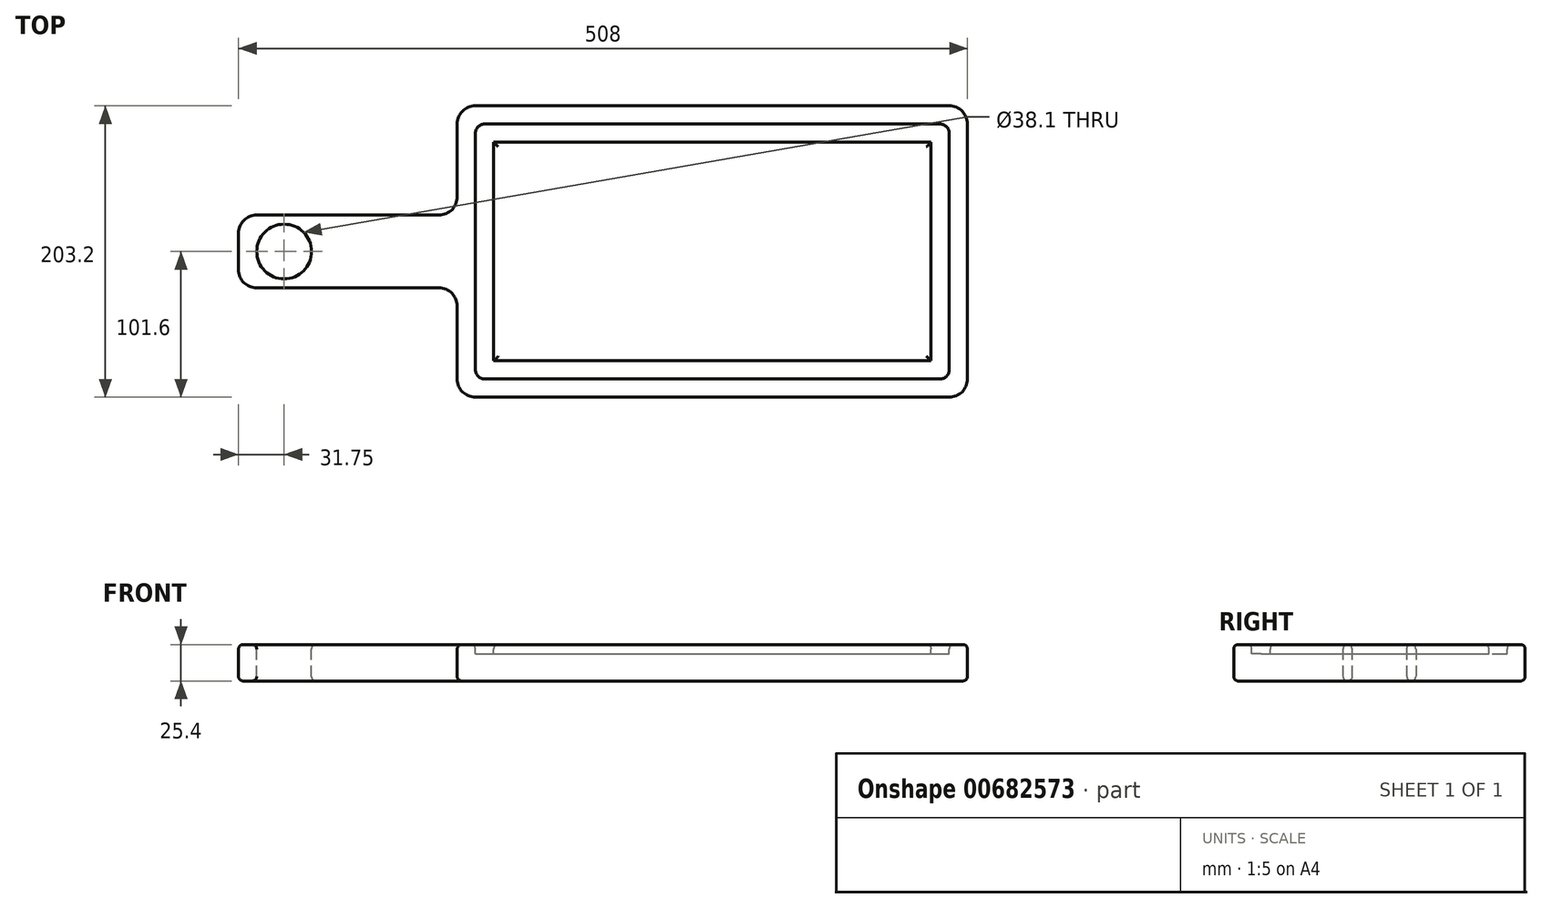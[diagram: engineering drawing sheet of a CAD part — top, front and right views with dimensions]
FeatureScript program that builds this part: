
annotation { "Feature Type Name" : "Feature", "Feature Type Description" : "" }
export const myFeature = defineFeature(function(context is Context, id is Id, definition is map)
    precondition{}
    {
        {
            var Q0;
            Q0=qCreatedBy(makeId("Top.planeOp"),FACE);
            var sketch = newSketch(context, id + "F0", { "sketchPlane" : qUnion([Q0])});
            skLineSegment(sketch, "E0.bottom", {"start": v(0, 0) * mm, "end": v(355.6, 0) * mm});
            skLineSegment(sketch, "E0.top", {"start": v(0, 203.2) * mm, "end": v(355.6, 203.2) * mm});
            skLineSegment(sketch, "E0.left", {"start": v(0, 0) * mm, "end": v(0, 203.2) * mm});
            skLineSegment(sketch, "E0.right", {"start": v(355.6, 0) * mm, "end": v(355.6, 203.2) * mm});
            skLineSegment(sketch, "E1.bottom", {"start": v(0, 127) * mm, "end": v(-152.4, 127) * mm});
            skLineSegment(sketch, "E1.top", {"start": v(0, 76.2) * mm, "end": v(-152.4, 76.2) * mm});
            skLineSegment(sketch, "E1.left", {"start": v(0, 127) * mm, "end": v(0, 76.2) * mm});
            skLineSegment(sketch, "E1.right", {"start": v(-152.4, 127) * mm, "end": v(-152.4, 76.2) * mm});
            skSolve(sketch);
        }
        {
            var Q0;
            {var subQ3=sQuery(id+"F0.wireOp",EDGE,"E0.bottom");Q0=makeQuery(id+"F0.imprint","IMPRINT",FACE,{"disambiguationData":[TD([[makeQuery(id+"F0.imprint","IMPRINT",EDGE,{"derivedFrom":subQ3}),1.0]])]});}
            var Q1;
            Q1=makeQuery(id+"F0.imprint","IMPRINT",FACE,{"disambiguationData":[TD([[makeQuery(id+"F0.imprint","IMPRINT",EDGE,{"derivedFrom":sQuery(id+"F0.wireOp",EDGE,"E1.bottom")}),1.0]])]});
            extrude(context, id + "F1", {"entities" : qUnion([Q0, Q1]), "depth" : 25.4 * mm, "offsetDistance" : 25.4 * mm});
        }
        {
            var Q0;
            Q0=makeQuery(id+"F1.opExtrude","CAP_FACE",FACE,{"disambiguationData":[OSD([sQuery(id+"F0.wireOp",EDGE,"E0.bottom"),sQuery(id+"F0.wireOp",EDGE,"E0.top"),sQuery(id+"F0.wireOp",EDGE,"E0.left"),sQuery(id+"F0.wireOp",EDGE,"E0.right"),sQuery(id+"F0.wireOp",EDGE,"E1.bottom"),sQuery(id+"F0.wireOp",EDGE,"E1.top"),sQuery(id+"F0.wireOp",EDGE,"E1.right")])],"isStart":false});
            var sketch = newSketch(context, id + "F2", { "sketchPlane" : qUnion([Q0])});
            skCircle(sketch, "E2", {"center": v(-120.65, 101.6) * mm, "radius": 19.05 * mm});
            skSolve(sketch);
        }
        {
            var Q0;
            Q0 = qSketchRegion(id + "F2", true);
            extrude(context, id + "F3", {"entities" : qUnion([Q0]), "operationType" : NewBodyOperationType.REMOVE, "oppositeDirection" : true, "depth" : 25.4 * mm, "offsetDistance" : 25.4 * mm});
        }
        {
            var Q0;
            Q0=makeQuery(id+"F1.opExtrude","CAP_FACE",FACE,{"disambiguationData":[OSD([sQuery(id+"F0.wireOp",EDGE,"E0.bottom"),sQuery(id+"F0.wireOp",EDGE,"E0.top"),sQuery(id+"F0.wireOp",EDGE,"E0.left"),sQuery(id+"F0.wireOp",EDGE,"E0.right"),sQuery(id+"F0.wireOp",EDGE,"E1.bottom"),sQuery(id+"F0.wireOp",EDGE,"E1.top"),sQuery(id+"F0.wireOp",EDGE,"E1.right")])],"isStart":false});
            var sketch = newSketch(context, id + "F4", { "sketchPlane" : qUnion([Q0])});
            skLineSegment(sketch, "E3.0", {"start": v(12.7, 12.7) * mm, "end": v(12.7, 76.2) * mm});
            skLineSegment(sketch, "E3.1", {"start": v(12.7, 127) * mm, "end": v(12.7, 190.5) * mm});
            skLineSegment(sketch, "E3.2", {"start": v(12.7, 190.5) * mm, "end": v(342.9, 190.5) * mm});
            skLineSegment(sketch, "E3.3", {"start": v(342.9, 12.7) * mm, "end": v(342.9, 190.5) * mm});
            skLineSegment(sketch, "E3.4", {"start": v(12.7, 12.7) * mm, "end": v(342.9, 12.7) * mm});
            skLineSegment(sketch, "E4", {"start": v(12.7, 127) * mm, "end": v(12.7, 76.2) * mm});
            skLineSegment(sketch, "E5.0", {"start": v(25.4, 127) * mm, "end": v(25.4, 177.8) * mm});
            skLineSegment(sketch, "E5.1", {"start": v(330.2, 25.4) * mm, "end": v(330.2, 177.8) * mm});
            skLineSegment(sketch, "E5.2", {"start": v(25.4, 25.4) * mm, "end": v(330.2, 25.4) * mm});
            skLineSegment(sketch, "E5.3", {"start": v(25.4, 177.8) * mm, "end": v(330.2, 177.8) * mm});
            skLineSegment(sketch, "E5.4", {"start": v(25.4, 25.4) * mm, "end": v(25.4, 76.2) * mm});
            skLineSegment(sketch, "E5.5", {"start": v(25.4, 127) * mm, "end": v(25.4, 76.2) * mm});
            skSolve(sketch);
        }
        {
            var Q0;
            Q0=makeQuery(id+"F4.imprint","IMPRINT",FACE,{"disambiguationData":[TD([[makeQuery(id+"F4.imprint","IMPRINT",EDGE,{"derivedFrom":sQuery(id+"F4.wireOp",EDGE,"E3.0")}),-1.0]])]});
            extrude(context, id + "F5", {"entities" : qUnion([Q0]), "operationType" : NewBodyOperationType.REMOVE, "oppositeDirection" : true, "depth" : 6.35 * mm, "offsetDistance" : 25.4 * mm});
        }
        {
            var Q0;
            Q0=makeQuery(id+"F5.boolean.opBoolean","COPY",EDGE,{"derivedFrom":makeQuery(id+"F5.opExtrude","SWEPT_EDGE",EDGE,{"disambiguationData":[OSD([sQuery(id+"F4.wireOp",EDGE,"E3.1"),sQuery(id+"F4.wireOp",EDGE,"E3.2")])]})});
            var Q1;
            Q1=makeQuery(id+"F5.boolean.opBoolean","COPY",EDGE,{"derivedFrom":makeQuery(id+"F5.opExtrude","SWEPT_EDGE",EDGE,{"disambiguationData":[OSD([sQuery(id+"F4.wireOp",EDGE,"E3.2"),sQuery(id+"F4.wireOp",EDGE,"E3.3")])]})});
            var Q2;
            Q2=makeQuery(id+"F5.boolean.opBoolean","COPY",EDGE,{"derivedFrom":makeQuery(id+"F5.opExtrude","SWEPT_EDGE",EDGE,{"disambiguationData":[OSD([sQuery(id+"F4.wireOp",EDGE,"E3.3"),sQuery(id+"F4.wireOp",EDGE,"E3.4")])]})});
            var Q3;
            Q3=makeQuery(id+"F5.boolean.opBoolean","COPY",EDGE,{"derivedFrom":makeQuery(id+"F5.opExtrude","SWEPT_EDGE",EDGE,{"disambiguationData":[OSD([sQuery(id+"F4.wireOp",EDGE,"E3.0"),sQuery(id+"F4.wireOp",EDGE,"E3.4")])]})});
            fillet(context, id + "F6", {"entities" : qUnion([Q0, Q1, Q2, Q3]), "radius" : 6.35 * mm, "tangentPropagation" : true, "allowEdgeOverflow" : false});
        }
        {
            var Q0;
            Q0=makeQuery(id+"F1.opExtrude","SWEPT_EDGE",EDGE,{"disambiguationData":[OSD([sQuery(id+"F0.wireOp",EDGE,"E0.bottom"),sQuery(id+"F0.wireOp",EDGE,"E0.left")])]});
            var Q1;
            Q1=makeQuery(id+"F1.opExtrude","SWEPT_EDGE",EDGE,{"disambiguationData":[OSD([sQuery(id+"F0.wireOp",EDGE,"E1.top"),sQuery(id+"F0.wireOp",EDGE,"E1.right")])]});
            var Q2;
            Q2=makeQuery(id+"F1.opExtrude","SWEPT_EDGE",EDGE,{"disambiguationData":[OSD([sQuery(id+"F0.wireOp",EDGE,"E1.bottom"),sQuery(id+"F0.wireOp",EDGE,"E1.right")])]});
            var Q3;
            Q3=makeQuery(id+"F1.opExtrude","SWEPT_EDGE",EDGE,{"disambiguationData":[OSD([sQuery(id+"F0.wireOp",EDGE,"E0.top"),sQuery(id+"F0.wireOp",EDGE,"E0.left")])]});
            var Q4;
            Q4=makeQuery(id+"F1.opExtrude","SWEPT_EDGE",EDGE,{"disambiguationData":[OSD([sQuery(id+"F0.wireOp",EDGE,"E0.top"),sQuery(id+"F0.wireOp",EDGE,"E0.right")])]});
            var Q5;
            Q5=makeQuery(id+"F1.opExtrude","SWEPT_EDGE",EDGE,{"disambiguationData":[OSD([sQuery(id+"F0.wireOp",EDGE,"E0.bottom"),sQuery(id+"F0.wireOp",EDGE,"E0.right")])]});
            fillet(context, id + "F7", {"entities" : qUnion([Q0, Q1, Q2, Q3, Q4, Q5]), "radius" : 12.7 * mm, "tangentPropagation" : true, "allowEdgeOverflow" : false});
        }
        {
            var Q0;
            Q0=makeQuery(id+"F1.opExtrude","SWEPT_EDGE",EDGE,{"disambiguationData":[OSD([sQuery(id+"F0.wireOp",EDGE,"E0.left"),sQuery(id+"F0.wireOp",EDGE,"E1.top"),sQuery(id+"F0.wireOp",EDGE,"E1.left")])]});
            var Q1;
            Q1=makeQuery(id+"F1.opExtrude","SWEPT_EDGE",EDGE,{"disambiguationData":[OSD([sQuery(id+"F0.wireOp",EDGE,"E0.left"),sQuery(id+"F0.wireOp",EDGE,"E1.bottom"),sQuery(id+"F0.wireOp",EDGE,"E1.left")])]});
            fillet(context, id + "F8", {"entities" : qUnion([Q0, Q1]), "radius" : 12.7 * mm, "tangentPropagation" : true, "allowEdgeOverflow" : false});
        }
        {
            var Q0;
            Q0=makeQuery(id+"F5.boolean.opBoolean","SPLIT",FACE,{"disambiguationData":[TD([makeQuery(id+"F5.opExtrude","SWEPT_FACE",FACE,{"disambiguationData":[OSD([sQuery(id+"F4.wireOp",EDGE,"E5.1")])]})])],"derivedFrom":makeQuery(id+"F1.opExtrude","CAP_FACE",FACE,{"disambiguationData":[OSD([sQuery(id+"F0.wireOp",EDGE,"E0.bottom"),sQuery(id+"F0.wireOp",EDGE,"E0.top"),sQuery(id+"F0.wireOp",EDGE,"E0.left"),sQuery(id+"F0.wireOp",EDGE,"E0.right"),sQuery(id+"F0.wireOp",EDGE,"E1.bottom"),sQuery(id+"F0.wireOp",EDGE,"E1.top"),sQuery(id+"F0.wireOp",EDGE,"E1.right")])],"isStart":false})});
            var Q1;
            {var subQ0=sQuery(id+"F0.wireOp",EDGE,"E1.right");var subQ1=sQuery(id+"F0.wireOp",EDGE,"E1.top");var subQ2=sQuery(id+"F0.wireOp",EDGE,"E1.bottom");var subQ3=sQuery(id+"F0.wireOp",EDGE,"E0.right");var subQ4=sQuery(id+"F0.wireOp",EDGE,"E0.bottom");var subQ5=sQuery(id+"F0.wireOp",EDGE,"E0.left");var subQ6=sQuery(id+"F0.wireOp",EDGE,"E0.top");Q1=makeQuery(id+"F5.boolean.opBoolean","SPLIT",FACE,{"disambiguationData":[TD([makeQuery(id+"F1.opExtrude","SWEPT_FACE",FACE,{"disambiguationData":[OSD([subQ4])]})])],"derivedFrom":makeQuery(id+"F1.opExtrude","CAP_FACE",FACE,{"disambiguationData":[OSD([subQ4,subQ6,subQ5,subQ3,subQ2,subQ1,subQ0])],"isStart":false})});}
            var Q2;
            Q2=makeQuery(id+"F1.opExtrude","CAP_FACE",FACE,{"disambiguationData":[OSD([sQuery(id+"F0.wireOp",EDGE,"E0.bottom"),sQuery(id+"F0.wireOp",EDGE,"E0.top"),sQuery(id+"F0.wireOp",EDGE,"E0.left"),sQuery(id+"F0.wireOp",EDGE,"E0.right"),sQuery(id+"F0.wireOp",EDGE,"E1.bottom"),sQuery(id+"F0.wireOp",EDGE,"E1.top"),sQuery(id+"F0.wireOp",EDGE,"E1.right")])],"isStart":true});
            fillet(context, id + "F9", {"entities" : qUnion([Q0, Q1, Q2]), "radius" : 3.17 * mm, "tangentPropagation" : true, "allowEdgeOverflow" : false});
        }
    });
